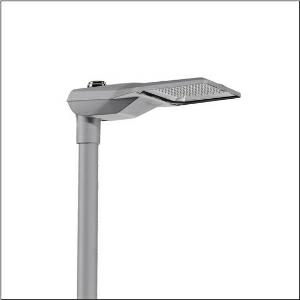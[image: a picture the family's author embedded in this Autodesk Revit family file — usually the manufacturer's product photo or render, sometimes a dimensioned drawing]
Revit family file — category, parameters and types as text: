
# Revit family: streetlight_sl_21_midi___st1_0a_5xe7d67n08nb_5be6
name_source: partatom
category: Lighting Fixtures
units: mm (PartAtom-declared; Revit-internal decimal feet)

## family parameters
Cut with Voids When Loaded = No
Host = Face
Light Source = No
Part Type = Normal
Room Calculation Point = No
Round Connector Dimension = Use Diameter
Shared = No

## types (1)
- --- (1 x LED, 20350 lm, 151.2 W, 2700K)
    Apparent Load = 151 VA
    CIE Flux Codes = 40 73 97 100 100
    Color Rendering = 70
    Color Temperature = 2700K
    Default Elevation = 1800 mm
    Description = Streetlight SL 21 midi, mast luminaire, primary light control with lens, of PMMA, primary optical cover: cover, of toughened safety glass, transparent, light distribution: ST1.0a, light emission: direct distribution, primary light characteristic: asymmetric, installation type: side-entry, LED, 3G 2.5mm², High Power LED, rated luminous flux: 20.350lm, luminous efficacy: 135lm/W, light colour: 727, colour temperature: 2700K, control gear: NEMA (7pin), control: overheat protection, pre-setting: linear dimming characteristic, constant luminous flux control, time-dependent luminous flux control, flexible luminous flux parameterisation, mains connection: 220..240V, AC, 50/60Hz, connection cable pre-assembled, cable length: 12,5m, wiring characteristics: H05VV-F, start of lifetime: 151W, end of service life: 157W, reduction: 70W, luminaire housing, of diecast aluminium (EN AC-44300), powder-coated, Siteco® metallic grey (DB 702S), corrosivity category C5 mid according to DIN EN ISO 12944, multi-level sealing system, sealing non-destructively replaceable, inclination adjustable: 0°, 5°, 10°, 15°, length: 644mm, width: 335mm, height: 110mm, spigot size: 42mm (side-entry), mounting height: 4..8m, protection rating (complete): IP66, insulation class (complete): insulation class I (protective earthing), certification: CE, ENEC, ENEC+, VDE, impact resistance: IK10, permissible operating ambient temperature for outdoor applications: -40..+50°C, standard-compliant lighting for roads and squares, packaging unit: 1 piece

Light Distribution: ST1.0a
    Height = 111 mm
    Lamp = 1 x LED
    Lamp Light Flux = 20350 lm
    Lamp Power = 151.2 W
    Lamp count = 1
    Length = 644 mm
    Luminous efficacy = 135 lm/W
    Manufacturer = Siteco
    ModVariant = No
    Model = 5XE7D67N08NB
    Number of Poles = 1
    OnlyDefault = Yes
    Power Factor = 1
    Product Name = Streetlight SL 21 midi | ST1.0a
    Product group = mast luminaire | pylon top
    ProductGroupID = 6100
    Protection Class = Protection class I
    Protection Degree = IP 66
    RLX_Detail_Level = 1
    RLX_Emergency_Light_Flux = 0 lm
    RLX_Emergency_Type = 0
    RLX_Emergency_Type_DB = No
    RlxData = <blob elided: 26729 chars, md5=451d1ed3>
    Socket = socket
    Standby Power = 0 W
    System Light Flux = 20350 lm
    System Power = 151 W
    Type Comments = factory setting: luminous flux: 100 % | dim-lin: 254 | 802 mA
    Type Image = l_1294377.jpg
    URL = http://relux.com
    VarID = @adj_156531
    Voltage = 0 V
    Weight = 0.00 kg
    Width = 336 mm

## geometry (parser evidence)
native form markers: Blend x4, Sweep x11
no freeform markers — native parametric forms only
